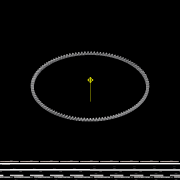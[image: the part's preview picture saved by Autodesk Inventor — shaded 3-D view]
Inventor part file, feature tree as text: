
AUTODESK INVENTOR PART (.ipt)
format: ipt  version: 2017 (Build 210142000, 142)  size: 1,811,456 bytes
history: native  units: mm
features: other x24, loft x2, pattern_circular x2, sketch x2, extrude x1
ambient origin geometry x6: Origin, XZ Plane, X Axis, Y Axis, Z Axis, Center Point
bodies: Solid1 (feature_tree)
feature tree (31):
  other  "Top Point"
  other  "Mesh Plane2"
  other  "Teeth Body"
  other  "Start Point"
  other  "Tooth Plane"
  other  "Start Sketch"
  other  "End Point"
  other  "3D Sketch Right"
  other  "End Plane Right"
  loft  "Loft Right"
  pattern_circular  "Circular Pattern Right"  [2 undecoded]
  other  "3D Sketch Left"
  other  "End Plane Left"
  loft  "Loft Left"
  pattern_circular  "Circular Pattern Left"  Angle=90.0deg  [1 undecoded]
  other  "Fix Body"
  extrude  "Extrusion1"  Depth=10.0mm
  other  "Mesh Plane"
  other  "Top Plane"
  other  "Teeth Body Sketch"
  other  "End Plane"
  other  "End Sketch"
  other  "Helical Curve Left"
  other  "End Sketch Left"
  other  "Body Sketch"
  sketch  "Sketch6"  dims[d0=302.26mm d1=301.497629mm]
  other  "Srf1"
  other  "Helical Curve Right"
  other  "End Sketch Right"
  sketch  "Sketch8"  dims[d2=302.895309mm d3=7.62mm d4=16.529941mm d5=90.0deg d7=414.205299mm d8=393.316689mm d9=1072.681211mm d11=7.8994mm d12=393.139419mm d15=373.313174mm d16=1018.126202mm d17=0.0mm d18=90.0deg d19=0.0mm d20=90.0deg d21=1190.0mm d22=360.0deg d26=314.208686mm d27=0.987905mm d28=302.26mm d29=-14.454072mm d30=393.139419mm d31=373.313174mm d32=1018.126202mm d35=0.0mm d37=0.0mm d39=0.0mm d40=90.0deg d41=1190.0mm d42=360.0deg d46=90.0deg d47=90.0deg d48=0.0mm d49=0.0mm d50=90.0deg d51=0.263999mm d52=0.0mm d53=0.0mm d54=0.0mm d56=18.022547mm d57=1212.66853mm d58=1204.73357mm d59=1150.993968mm d60=1143.462569mm d61=1150.993968mm d62=1143.462569mm d63=90.0deg d64=90.0deg d65=314.208686mm d66=31.5mm d67=302.26mm d68=-14.454072mm d69=0.987905mm d70=373.313174mm d71=1018.126202mm d72=393.139419mm d73=1143.462569mm d74=1150.993968mm d75=0.0mm d76=90.0deg d77=0.0mm d78=90.0deg d79=0.0mm d80=90.0deg d81=1190.0mm d82=360.0deg d84=10.0mm d85=20.0mm d86=20.0mm d87=10.0mm d88=0.0mm d89=0.0mm d90=25.4mm d91=0.0mm d92=286.4104mm]
  other  "Pitch Diameter"
note: 3 required parameter values undecoded (feature->parameter linkage not recoverable at this tier; creation-order binding heuristic only, values carry confidence <= 0.55)
